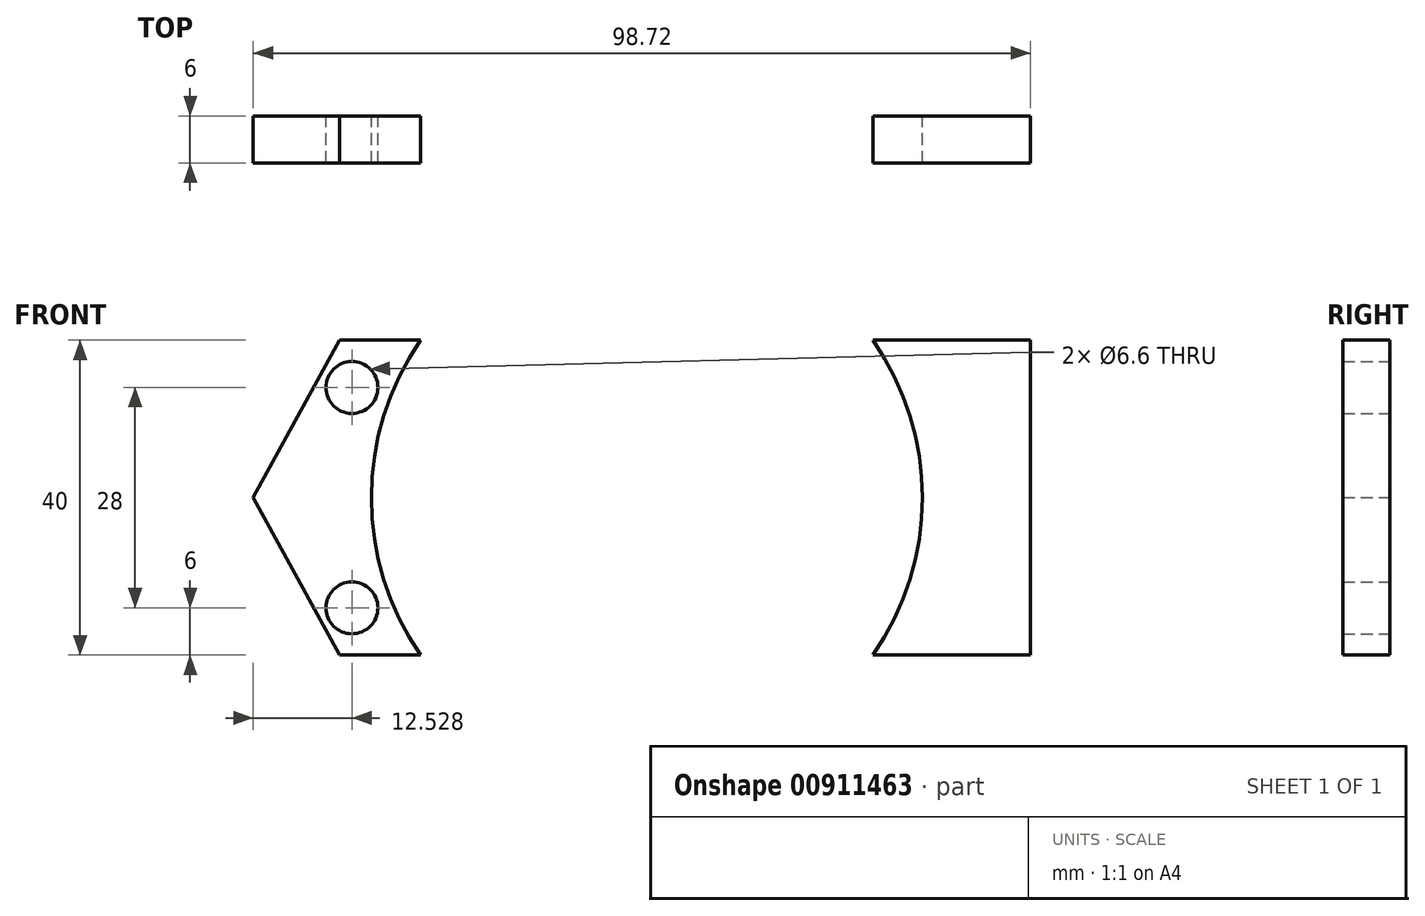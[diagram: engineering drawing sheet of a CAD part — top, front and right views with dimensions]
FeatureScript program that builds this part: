
annotation { "Feature Type Name" : "Feature", "Feature Type Description" : "" }
export const myFeature = defineFeature(function(context is Context, id is Id, definition is map)
    precondition{}
    {
        {
            var Q0;
            Q0=qCreatedBy(makeId("Front.planeOp"),FACE);
            var sketch = newSketch(context, id + "F0", { "sketchPlane" : qUnion([Q0])});
            skArc(sketch, "E0", {"start": v(-28.7, 20) * mm, "mid": v(-34.97, 0) * mm, "end": v(-28.7, -20) * mm});
            skArc(sketch, "E1", {"start": v(-34.61, 20) * mm, "mid": v(-39.97, 0) * mm, "end": v(-34.61, -20) * mm});
            skPoint(sketch, "E2", {"position": v(-18, 30) * mm});
            skPoint(sketch, "E3", {"position": v(-34.05, 8) * mm});
            skPoint(sketch, "E4", {"position": v(-34.05, -8) * mm});
            skPoint(sketch, "E5", {"position": v(-18, -30) * mm});
            skLineSegment(sketch, "E6", {"start": v(-38.99, 20) * mm, "end": v(-49.97, 0) * mm});
            skLineSegment(sketch, "E7", {"start": v(-18, -35.7) * mm, "end": v(-18, -40) * mm});
            skLineSegment(sketch, "E8", {"start": v(-38.99, -20) * mm, "end": v(-49.97, 0) * mm});
            skPoint(sketch, "E9", {"position": v(28.75, 20) * mm});
            skPoint(sketch, "E10", {"position": v(28.75, -20) * mm});
            skLineSegment(sketch, "E11", {"start": v(28.75, 20) * mm, "end": v(48.75, 20) * mm});
            skLineSegment(sketch, "E12", {"start": v(48.75, 20) * mm, "end": v(48.75, -20) * mm});
            skLineSegment(sketch, "E13", {"start": v(28.75, -20) * mm, "end": v(48.75, -20) * mm});
            skPoint(sketch, "E14", {"position": v(-37.44, 14) * mm});
            skPoint(sketch, "E15", {"position": v(-37.44, -14) * mm});
            skArc(sketch, "E16.trimOffspring", {"start": v(28.75, -20) * mm, "mid": v(35.03, 0) * mm, "end": v(28.75, 20) * mm});
            skArc(sketch, "E17.trimOffspring", {"start": v(34.67, -20) * mm, "mid": v(40.03, 0) * mm, "end": v(34.67, 20) * mm});
            skLineSegment(sketch, "E18", {"start": v(48.75, 20) * mm, "end": v(28.75, 20) * mm});
            skLineSegment(sketch, "E19", {"start": v(48.75, -20) * mm, "end": v(28.75, -20) * mm});
            skPoint(sketch, "E20.end.orphan", {"position": v(-28, 40) * mm});
            skPoint(sketch, "E21.orphan", {"position": v(-18, 40) * mm});
            skPoint(sketch, "E22.start.orphan", {"position": v(-28, -40) * mm});
            skLineSegment(sketch, "E23.trimOffspring", {"start": v(-28.7, 20) * mm, "end": v(-38.99, 20) * mm});
            skLineSegment(sketch, "E24.trimOffspring", {"start": v(-28.7, -20) * mm, "end": v(-38.99, -20) * mm});
            skSolve(sketch);
        }
        {
            var Q0;
            Q0 = qSketchRegion(id + "F0", true);
            extrude(context, id + "F1", {"entities" : qUnion([Q0]), "depth" : 6 * mm, "offsetDistance" : 25 * mm});
        }
        {
            var Q0;
            Q0=sQuery(id+"F0.wireOp",VERTEX,"E15");
            var Q1;
            Q1=sQuery(id+"F0.wireOp",VERTEX,"E14");
            var Q2;
            Q2=makeQuery(id+"F1.opExtrude","SWEPT_BODY",BODY,{"disambiguationData":[OSD([sQuery(id+"F0.wireOp",EDGE,"E0"),sQuery(id+"F0.wireOp",EDGE,"48NImiS3-Kji4-2mcl-x8IC-T8MfFKJ4dPNQ"),sQuery(id+"F0.wireOp",EDGE,"E20"),sQuery(id+"F0.wireOp",EDGE,"E6"),sQuery(id+"F0.wireOp",EDGE,"E7"),sQuery(id+"F0.wireOp",EDGE,"E22"),sQuery(id+"F0.wireOp",EDGE,"E8")])]});
            hole(context, id + "F2", {"style" : HoleStyle.SIMPLE, "endStyle" : HoleEndStyle.THROUGH, "oppositeDirection" : true, "standardTappedOrClearance" : lookupTablePath({ "fit" : "Normal", "standard" : "ISO", "size" : "M6", "type" : "Clearance" }), "standardBlindInLast" : lookupTablePath({ "fit" : "Normal", "standard" : "ISO", "size" : "M6", "type" : "Clearance" }), "holeDiameter" : 6.6 * mm, "majorDiameter" : 5 * mm, "isTappedThrough" : true, "tappedDepth" : 11.5 * mm, "tapClearance" : 3, "startFromSketch" : true, "locations" : qUnion([Q0, Q1]), "scope" : qUnion([Q2])});
        }
    });
